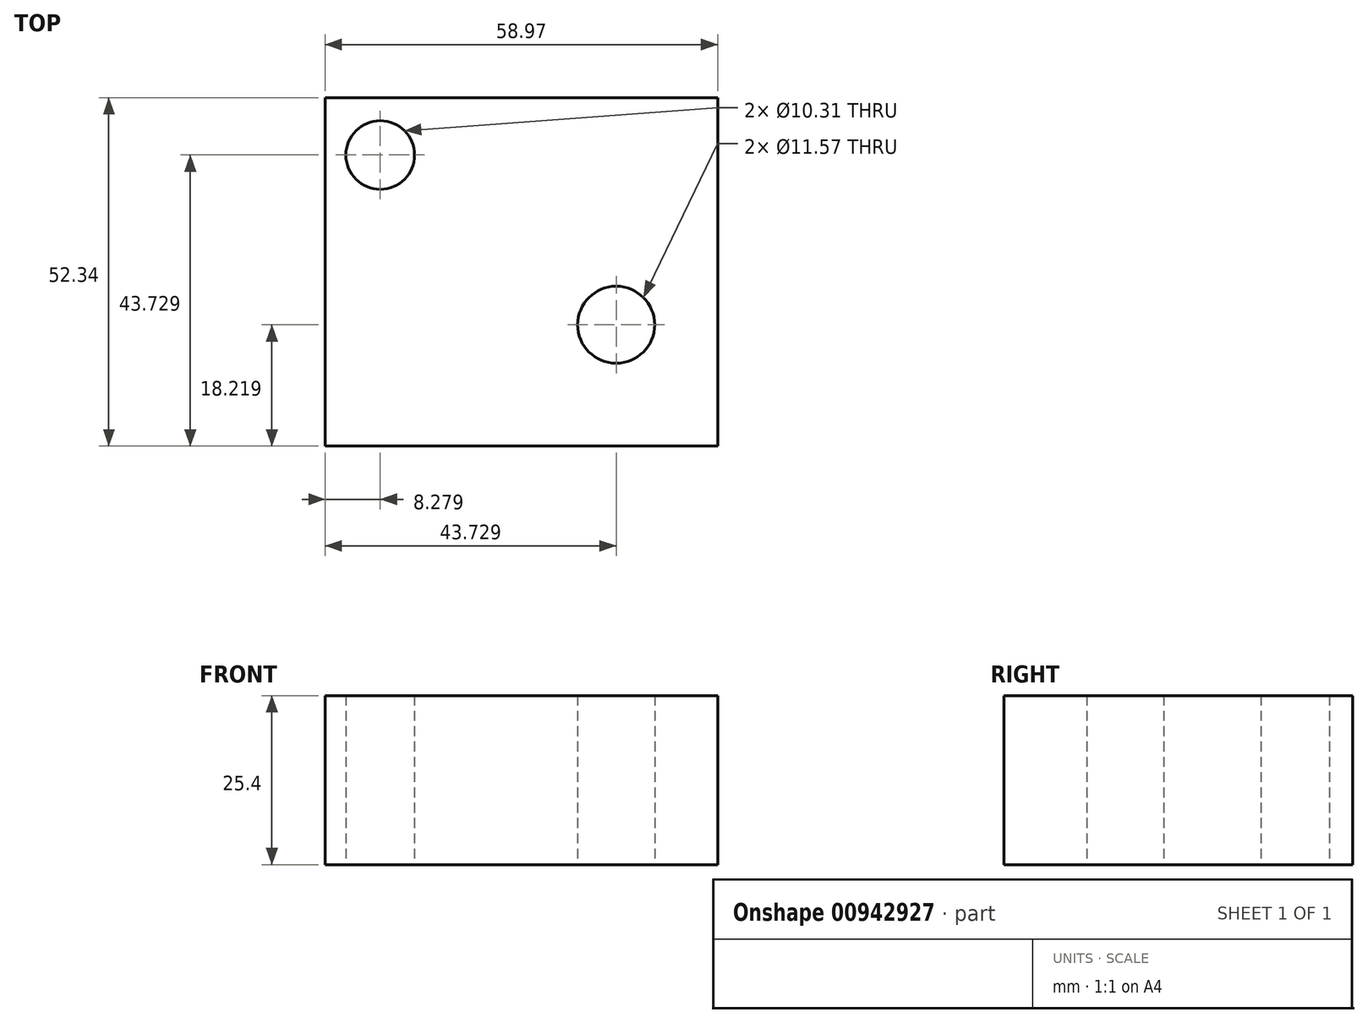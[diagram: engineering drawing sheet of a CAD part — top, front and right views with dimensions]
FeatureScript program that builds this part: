
annotation { "Feature Type Name" : "Feature", "Feature Type Description" : "" }
export const myFeature = defineFeature(function(context is Context, id is Id, definition is map)
    precondition{}
    {
        {
            var Q0;
            Q0=qCreatedBy(makeId("Top.planeOp"),FACE);
            var sketch = newSketch(context, id + "F0", { "sketchPlane" : qUnion([Q0])});
            skLineSegment(sketch, "E0.bottom", {"start": v(-32.63, 26.17) * mm, "end": v(26.34, 26.17) * mm});
            skLineSegment(sketch, "E0.top", {"start": v(-32.63, -26.17) * mm, "end": v(26.34, -26.17) * mm});
            skLineSegment(sketch, "E0.left", {"start": v(-32.63, 26.17) * mm, "end": v(-32.63, -26.17) * mm});
            skLineSegment(sketch, "E0.right", {"start": v(26.34, 26.17) * mm, "end": v(26.34, -26.17) * mm});
            skPoint(sketch, "E0.middle", {"position": v(-3.15, 0) * mm});
            skCircle(sketch, "E1", {"center": v(-24.35, 17.56) * mm, "radius": 5.15 * mm});
            skCircle(sketch, "E2", {"center": v(11.1, -7.95) * mm, "radius": 5.79 * mm});
            skSolve(sketch);
        }
        {
            var Q0;
            Q0=makeQuery(id+"F0.imprint","IMPRINT",FACE,{"disambiguationData":[TD([[makeQuery(id+"F0.imprint","IMPRINT",EDGE,{"derivedFrom":sQuery(id+"F0.wireOp",EDGE,"E0.bottom")}),-1.0]])]});
            extrude(context, id + "F1", {"entities" : qUnion([Q0]), "depth" : 25.4 * mm, "offsetDistance" : 25.4 * mm});
        }
    });
